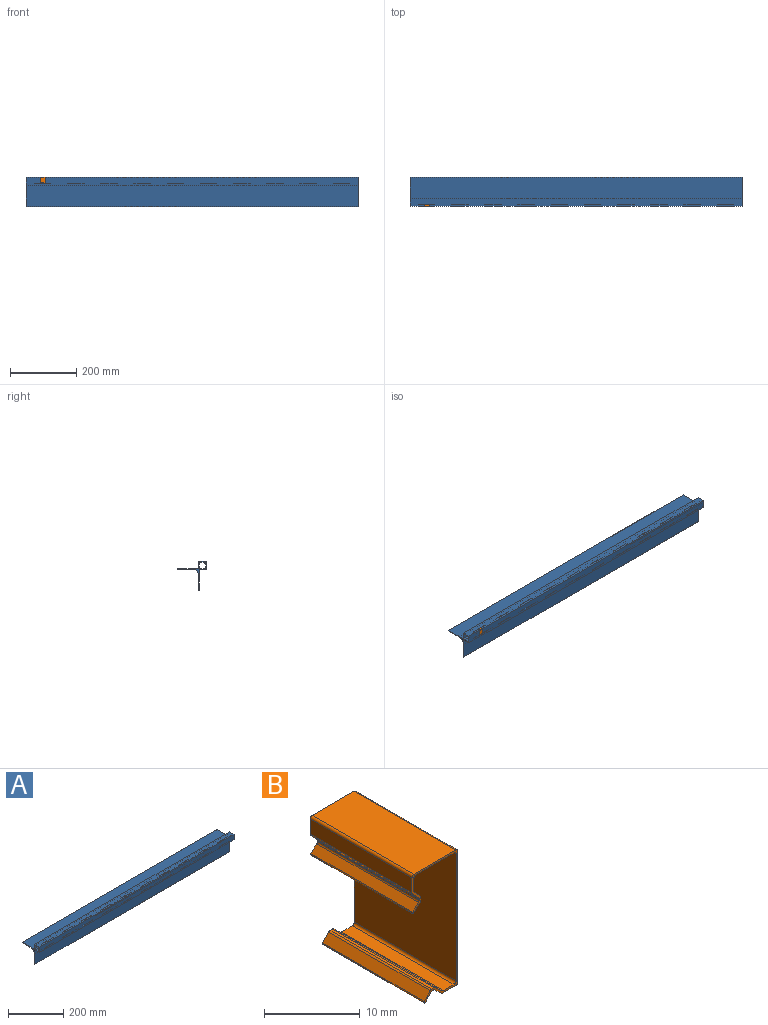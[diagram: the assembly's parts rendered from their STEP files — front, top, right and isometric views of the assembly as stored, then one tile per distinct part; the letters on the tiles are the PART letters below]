
ASSEMBLY  parts=2 mates=1
PART A: 101 faces, bbox 1000x88x88 mm
  f0: plane 1000x24mm, normal (0,0,1), area 23400mm2, adj f1,f9,f19,f20,f25,f26,f27,f28
  f1: plane 1000x24mm, normal (0,-1,0), area 23400mm2, adj f0,f18,f19,f20,f21,f22,f23,f24
  f2: plane 1000x63.2mm, normal (0,-1,0), area 63200mm2, adj f3,f18,f19,f20
  f3: cylinder r=0.8mm len=1000mm, axis (-1,0,0), area 2513.3mm2, adj f2,f4,f19,f20
  f4: plane 1000x45.6mm, normal (0,1,0), area 45600mm2, adj f3,f5,f19,f20
  f5: cylinder r=18mm len=1000mm, axis (-1,0,0), area 28274.3mm2, adj f4,f6,f19,f20
  f6: plane 1000x45.6mm, normal (0,0,-1), area 45600mm2, adj f5,f7,f19,f20
  f7: cylinder r=0.8mm len=1000mm, axis (-1,0,0), area 2513.3mm2, adj f6,f8,f19,f20
  f8: plane 1000x63.2mm, normal (0,0,1), area 63200mm2, adj f7,f9,f19,f20
  f9: plane 1000x22mm, normal (0,1,0), area 22000mm2, adj f0,f8,f19,f20
  f10: cylinder r=4mm len=1000mm, axis (-1,0,0), area 6283.2mm2, adj f11,f17,f19,f20
  f11: plane 1000x12mm, normal (0,0,1), area 12000mm2, adj f10,f12,f19,f20
  f12: cylinder r=4mm len=1000mm, axis (-1,0,0), area 6283.2mm2, adj f11,f13,f19,f20,f22,f30,f38,f46
  f13: plane 1000x12mm, normal (0,1,0), area 11400mm2, adj f12,f14,f19,f20,f21,f23,f24,f29
  f14: cylinder r=4mm len=1000mm, axis (-1,0,0), area 6283.2mm2, adj f13,f15,f19,f20,f26,f34,f42,f50
  f15: plane 1000x12mm, normal (0,0,-1), area 11400mm2, adj f14,f16,f19,f20,f25,f27,f28,f33
  f16: cylinder r=4mm len=1000mm, axis (-1,0,0), area 6283.2mm2, adj f15,f17,f19,f20
  f17: plane 1000x12mm, normal (0,-1,0), area 12000mm2, adj f10,f16,f19,f20
  f18: plane 1000x22mm, normal (0,0,-1), area 22000mm2, adj f1,f2,f19,f20
  f19: plane 88x88mm, normal (1,0,0), area 463.4mm2, adj f0,f1,f2,f3,f4,f5,f6,f7
  f20: plane 88x88mm, normal (-1,0,0), area 463.4mm2, adj f0,f1,f2,f3,f4,f5,f6,f7
  f21: plane 2x1.2mm, normal (1,0,0), area 2.4mm2, adj f1,f13,f22,f24
  f22: plane 50x2mm, normal (0,0,1), area 100mm2, adj f1,f12,f21,f23
  f23: plane 2x1.2mm, normal (-1,0,0), area 2.4mm2, adj f1,f13,f22,f24
  f24: plane 50x2mm, normal (0,0,-1), area 100mm2, adj f1,f13,f21,f23
  f25: plane 2x1.2mm, normal (1,0,0), area 2.4mm2, adj f0,f15,f26,f28
  f26: plane 50x2mm, normal (0,1,0), area 100mm2, adj f0,f14,f25,f27
  f27: plane 2x1.2mm, normal (-1,0,0), area 2.4mm2, adj f0,f15,f26,f28
  f28: plane 50x2mm, normal (0,-1,0), area 100mm2, adj f0,f15,f25,f27
  f29: plane 2x1.2mm, normal (1,0,0), area 2.4mm2, adj f1,f13,f30,f32
  f30: plane 50x2mm, normal (0,0,1), area 100mm2, adj f1,f12,f29,f31
  f31: plane 2x1.2mm, normal (-1,0,0), area 2.4mm2, adj f1,f13,f30,f32
  f32: plane 50x2mm, normal (0,0,-1), area 100mm2, adj f1,f13,f29,f31
  f33: plane 2x1.2mm, normal (1,0,0), area 2.4mm2, adj f0,f15,f34,f36
  f34: plane 50x2mm, normal (0,1,0), area 100mm2, adj f0,f14,f33,f35
  f35: plane 2x1.2mm, normal (-1,0,0), area 2.4mm2, adj f0,f15,f34,f36
  f36: plane 50x2mm, normal (0,-1,0), area 100mm2, adj f0,f15,f33,f35
  f37: plane 2x1.2mm, normal (1,0,0), area 2.4mm2, adj f1,f13,f38,f40
  f38: plane 50x2mm, normal (0,0,1), area 100mm2, adj f1,f12,f37,f39
  f39: plane 2x1.2mm, normal (-1,0,0), area 2.4mm2, adj f1,f13,f38,f40
  f40: plane 50x2mm, normal (0,0,-1), area 100mm2, adj f1,f13,f37,f39
  f41: plane 2x1.2mm, normal (1,0,0), area 2.4mm2, adj f0,f15,f42,f44
  f42: plane 50x2mm, normal (0,1,0), area 100mm2, adj f0,f14,f41,f43
  f43: plane 2x1.2mm, normal (-1,0,0), area 2.4mm2, adj f0,f15,f42,f44
  f44: plane 50x2mm, normal (0,-1,0), area 100mm2, adj f0,f15,f41,f43
  f45: plane 2x1.2mm, normal (1,0,0), area 2.4mm2, adj f1,f13,f46,f48
  f46: plane 50x2mm, normal (0,0,1), area 100mm2, adj f1,f12,f45,f47
  f47: plane 2x1.2mm, normal (-1,0,0), area 2.4mm2, adj f1,f13,f46,f48
  f48: plane 50x2mm, normal (0,0,-1), area 100mm2, adj f1,f13,f45,f47
  f49: plane 2x1.2mm, normal (1,0,0), area 2.4mm2, adj f0,f15,f50,f52
  f50: plane 50x2mm, normal (0,1,0), area 100mm2, adj f0,f14,f49,f51
  f51: plane 2x1.2mm, normal (-1,0,0), area 2.4mm2, adj f0,f15,f50,f52
  f52: plane 50x2mm, normal (0,-1,0), area 100mm2, adj f0,f15,f49,f51
  f53: plane 2x1.2mm, normal (1,0,0), area 2.4mm2, adj f1,f13,f54,f56
  f54: plane 50x2mm, normal (0,0,1), area 100mm2, adj f1,f12,f53,f55
  f55: plane 2x1.2mm, normal (-1,0,0), area 2.4mm2, adj f1,f13,f54,f56
  f56: plane 50x2mm, normal (0,0,-1), area 100mm2, adj f1,f13,f53,f55
  f57: plane 2x1.2mm, normal (1,0,0), area 2.4mm2, adj f0,f15,f58,f60
  f58: plane 50x2mm, normal (0,1,0), area 100mm2, adj f0,f14,f57,f59
  f59: plane 2x1.2mm, normal (-1,0,0), area 2.4mm2, adj f0,f15,f58,f60
  f60: plane 50x2mm, normal (0,-1,0), area 100mm2, adj f0,f15,f57,f59
  f61: plane 2x1.2mm, normal (1,0,0), area 2.4mm2, adj f1,f13,f62,f64
  f62: plane 50x2mm, normal (0,0,1), area 100mm2, adj f1,f12,f61,f63
  f63: plane 2x1.2mm, normal (-1,0,0), area 2.4mm2, adj f1,f13,f62,f64
  f64: plane 50x2mm, normal (0,0,-1), area 100mm2, adj f1,f13,f61,f63
  f65: plane 2x1.2mm, normal (1,0,0), area 2.4mm2, adj f0,f15,f66,f68
  f66: plane 50x2mm, normal (0,1,0), area 100mm2, adj f0,f14,f65,f67
  f67: plane 2x1.2mm, normal (-1,0,0), area 2.4mm2, adj f0,f15,f66,f68
  f68: plane 50x2mm, normal (0,-1,0), area 100mm2, adj f0,f15,f65,f67
  f69: plane 2x1.2mm, normal (1,0,0), area 2.4mm2, adj f1,f13,f70,f72
  f70: plane 50x2mm, normal (0,0,1), area 100mm2, adj f1,f12,f69,f71
  f71: plane 2x1.2mm, normal (-1,0,0), area 2.4mm2, adj f1,f13,f70,f72
  f72: plane 50x2mm, normal (0,0,-1), area 100mm2, adj f1,f13,f69,f71
  f73: plane 2x1.2mm, normal (1,0,0), area 2.4mm2, adj f0,f15,f74,f76
  f74: plane 50x2mm, normal (0,1,0), area 100mm2, adj f0,f14,f73,f75
  f75: plane 2x1.2mm, normal (-1,0,0), area 2.4mm2, adj f0,f15,f74,f76
  f76: plane 50x2mm, normal (0,-1,0), area 100mm2, adj f0,f15,f73,f75
  f77: plane 2x1.2mm, normal (1,0,0), area 2.4mm2, adj f1,f13,f78,f80
  f78: plane 50x2mm, normal (0,0,1), area 100mm2, adj f1,f12,f77,f79
  f79: plane 2x1.2mm, normal (-1,0,0), area 2.4mm2, adj f1,f13,f78,f80
  f80: plane 50x2mm, normal (0,0,-1), area 100mm2, adj f1,f13,f77,f79
  f81: plane 2x1.2mm, normal (1,0,0), area 2.4mm2, adj f0,f15,f82,f84
  f82: plane 50x2mm, normal (0,1,0), area 100mm2, adj f0,f14,f81,f83
  f83: plane 2x1.2mm, normal (-1,0,0), area 2.4mm2, adj f0,f15,f82,f84
  f84: plane 50x2mm, normal (0,-1,0), area 100mm2, adj f0,f15,f81,f83
  f85: plane 2x1.2mm, normal (1,0,0), area 2.4mm2, adj f1,f13,f86,f88
  f86: plane 50x2mm, normal (0,0,1), area 100mm2, adj f1,f12,f85,f87
  f87: plane 2x1.2mm, normal (-1,0,0), area 2.4mm2, adj f1,f13,f86,f88
  f88: plane 50x2mm, normal (0,0,-1), area 100mm2, adj f1,f13,f85,f87
  f89: plane 2x1.2mm, normal (1,0,0), area 2.4mm2, adj f0,f15,f90,f92
  f90: plane 50x2mm, normal (0,1,0), area 100mm2, adj f0,f14,f89,f91
  f91: plane 2x1.2mm, normal (-1,0,0), area 2.4mm2, adj f0,f15,f90,f92
  f92: plane 50x2mm, normal (0,-1,0), area 100mm2, adj f0,f15,f89,f91
  f93: plane 2x1.2mm, normal (1,0,0), area 2.4mm2, adj f1,f13,f94,f96
  f94: plane 50x2mm, normal (0,0,1), area 100mm2, adj f1,f12,f93,f95
  f95: plane 2x1.2mm, normal (-1,0,0), area 2.4mm2, adj f1,f13,f94,f96
  f96: plane 50x2mm, normal (0,0,-1), area 100mm2, adj f1,f13,f93,f95
  f97: plane 2x1.2mm, normal (1,0,0), area 2.4mm2, adj f0,f15,f98,f100
  f98: plane 50x2mm, normal (0,1,0), area 100mm2, adj f0,f14,f97,f99
  f99: plane 2x1.2mm, normal (-1,0,0), area 2.4mm2, adj f0,f15,f98,f100
  f100: plane 50x2mm, normal (0,-1,0), area 100mm2, adj f0,f15,f97,f99
PART B: 42 faces, bbox 6.8x15x17.3 mm
  f0: cylinder r=0.3mm len=15mm, axis (0,1,0), area 3.4mm2, adj f1,f39,f40,f41
  f1: plane 15x1.58mm, normal (1,0,0), area 23.7mm2, adj f0,f2,f40,f41
  f2: cylinder r=0.3mm len=15mm, axis (0,1,0), area 7.1mm2, adj f1,f3,f40,f41
  f3: plane 15x5.65mm, normal (0,0,-1), area 84.7mm2, adj f2,f4,f40,f41
  f4: cylinder r=0.3mm len=15mm, axis (0,1,0), area 7.1mm2, adj f3,f5,f40,f41
  f5: plane 16.2x15mm, normal (-1,0,0), area 243mm2, adj f4,f6,f40,f41
  f6: cylinder r=0.3mm len=15mm, axis (0,1,0), area 7.1mm2, adj f5,f7,f40,f41
  f7: plane 15x1.58mm, normal (0,0,1), area 23.7mm2, adj f6,f8,f40,f41
  f8: cylinder r=0.3mm len=15mm, axis (0,1,0), area 3.4mm2, adj f7,f9,f40,f41
  f9: plane 15x0.94mm, normal (0.69,0,0.73), area 19.4mm2, adj f8,f10,f40,f41
  f10: cylinder r=0.3mm len=15mm, axis (0,1,0), area 3.4mm2, adj f9,f11,f40,f41
  f11: plane 15x0.35mm, normal (0,0,1), area 5.3mm2, adj f10,f12,f40,f41
  f12: cylinder r=0.3mm len=15mm, axis (0,1,0), area 3.7mm2, adj f11,f13,f40,f41
  f13: plane 15x0.94mm, normal (-0.73,0,0.69), area 19.4mm2, adj f12,f14,f40,f41
  f14: cylinder r=0.12mm len=15mm, axis (0,1,0), area 5.9mm2, adj f13,f15,f40,f41
  f15: plane 15x0.86mm, normal (0.73,0,-0.69), area 17.8mm2, adj f14,f16,f40,f41
  f16: cylinder r=0.3mm len=15mm, axis (0,1,0), area 3.7mm2, adj f15,f17,f40,f41
  f17: plane 15x0.15mm, normal (0,0,-1), area 2.2mm2, adj f16,f18,f40,f41
  f18: cylinder r=0.3mm len=15mm, axis (0,1,0), area 3.4mm2, adj f17,f19,f40,f41
  f19: plane 15x0.94mm, normal (-0.69,0,-0.73), area 19.4mm2, adj f18,f20,f40,f41
  f20: cylinder r=0.3mm len=15mm, axis (0,1,0), area 3.4mm2, adj f19,f21,f40,f41
  f21: plane 15x1.93mm, normal (0,0,-1), area 29mm2, adj f20,f22,f40,f41
  f22: cylinder r=0.3mm len=15mm, axis (0,1,0), area 7.1mm2, adj f21,f23,f40,f41
  f23: plane 16.7x15mm, normal (1,0,0), area 250.5mm2, adj f22,f24,f40,f41
  f24: cylinder r=0.3mm len=15mm, axis (0,1,0), area 7.1mm2, adj f23,f25,f40,f41
  f25: plane 15x6.15mm, normal (0,0,1), area 92.2mm2, adj f24,f26,f40,f41
  f26: cylinder r=0.3mm len=15mm, axis (0,1,0), area 7.1mm2, adj f25,f27,f40,f41
  f27: plane 15x1.93mm, normal (-1,0,0), area 29mm2, adj f26,f28,f40,f41
  f28: cylinder r=0.3mm len=15mm, axis (0,1,0), area 3.4mm2, adj f27,f29,f40,f41
  f29: plane 15x0.94mm, normal (-0.73,0,-0.69), area 19.4mm2, adj f28,f30,f40,f41
  f30: cylinder r=0.3mm len=15mm, axis (0,1,0), area 3.4mm2, adj f29,f31,f40,f41
  f31: plane 15x0.15mm, normal (-1,0,0), area 2.2mm2, adj f30,f32,f40,f41
  f32: cylinder r=0.3mm len=15mm, axis (0,1,0), area 3.7mm2, adj f31,f33,f40,f41
  f33: plane 15x0.86mm, normal (-0.69,0,0.73), area 17.8mm2, adj f32,f34,f40,f41
  f34: cylinder r=0.12mm len=15mm, axis (0,1,0), area 5.9mm2, adj f33,f35,f40,f41
  f35: plane 15x0.94mm, normal (0.69,0,-0.73), area 19.4mm2, adj f34,f36,f40,f41
  f36: cylinder r=0.3mm len=15mm, axis (0,1,0), area 3.7mm2, adj f35,f37,f40,f41
  f37: plane 15x0.35mm, normal (1,0,0), area 5.3mm2, adj f36,f38,f40,f41
  f38: cylinder r=0.3mm len=15mm, axis (0,1,0), area 3.4mm2, adj f37,f39,f40,f41
  f39: plane 15x0.94mm, normal (0.73,0,0.69), area 19.4mm2, adj f0,f38,f40,f41
  f40: plane 17.3x6.75mm, normal (0,-1,0), area 8.7mm2, adj f0,f1,f2,f3,f4,f5,f6,f7
  f41: plane 17.3x6.75mm, normal (0,1,0), area 8.7mm2, adj f0,f1,f2,f3,f4,f5,f6,f7
PLACE A at identity fixed
PLACE B rot(axis=(0,0,-1),90deg) t=(57.5,-0.75,0.27)mm
MATE parallel B.f27 <-> A.f26  axis (0,1,0) through (50,6,-1)mm
